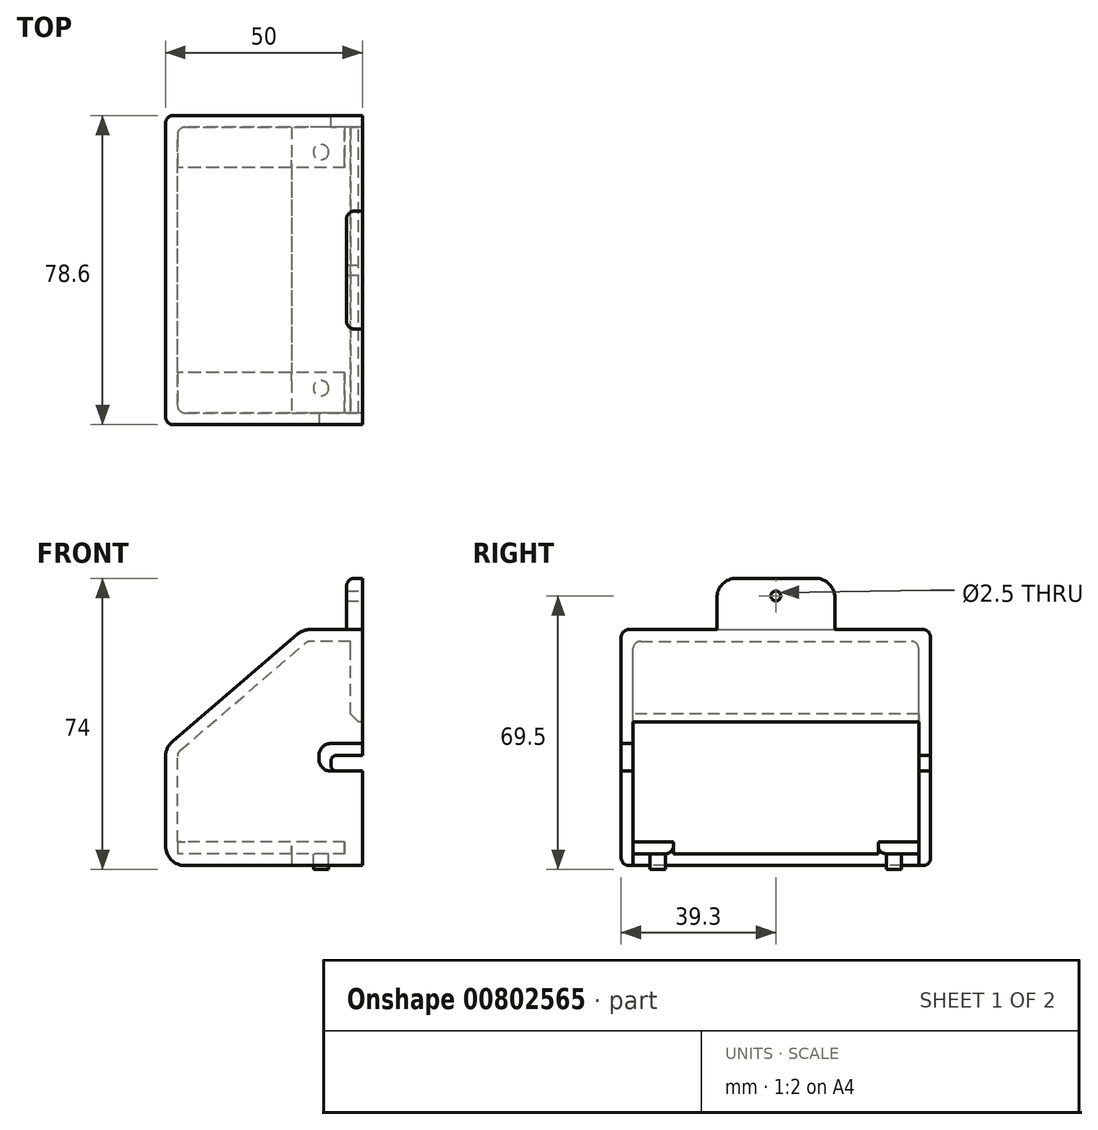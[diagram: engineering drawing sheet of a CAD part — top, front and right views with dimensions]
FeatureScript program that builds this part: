
annotation { "Feature Type Name" : "Feature", "Feature Type Description" : "" }
export const myFeature = defineFeature(function(context is Context, id is Id, definition is map)
    precondition{}
    {
        {
            var Q0;
            Q0=qCreatedBy(makeId("Front.planeOp"),FACE);
            var sketch = newSketch(context, id + "F0", { "sketchPlane" : qUnion([Q0])});
            skLineSegment(sketch, "E0", {"start": v(0, 0) * mm, "end": v(-50, 0) * mm});
            skLineSegment(sketch, "E1", {"start": v(-50, 0) * mm, "end": v(-50, 30) * mm});
            skLineSegment(sketch, "E2", {"start": v(0, 0) * mm, "end": v(0, 60) * mm});
            skLineSegment(sketch, "E3", {"start": v(0, 60) * mm, "end": v(-15, 60) * mm});
            skLineSegment(sketch, "E4", {"start": v(-50, 30) * mm, "end": v(-15, 60) * mm});
            skSolve(sketch);
        }
        {
            var Q0;
            Q0 = qSketchRegion(id + "F0", true);
            extrude(context, id + "F1", {"entities" : qUnion([Q0]), "depth" : 78.6 * mm, "offsetDistance" : 25 * mm});
        }
        {
            var Q0;
            Q0=qCreatedBy(makeId("Front.planeOp"),FACE);
            cPlane(context, id + "F2", {"entities" : qUnion([Q0]), "cplaneType" : CPlaneType.OFFSET, "offset" : 3 * mm, "width" : 150 * mm, "height" : 150 * mm});
        }
        {
            var Q0;
            Q0=qCreatedBy(id+"F2.planeOp",FACE);
            var sketch = newSketch(context, id + "F3", { "sketchPlane" : qUnion([Q0])});
            skLineSegment(sketch, "E5", {"start": v(0, 0) * mm, "end": v(0, 3) * mm, "construction": true});
            skLineSegment(sketch, "E6", {"start": v(0, 3) * mm, "end": v(-47, 3) * mm});
            skLineSegment(sketch, "E7", {"start": v(0, 3) * mm, "end": v(0, 36.5) * mm});
            skLineSegment(sketch, "E8", {"start": v(0, 36.5) * mm, "end": v(-3, 36.5) * mm});
            skLineSegment(sketch, "E9", {"start": v(-3, 36.5) * mm, "end": v(-3, 57) * mm});
            skLineSegment(sketch, "E10.0", {"start": v(-47, 28.62) * mm, "end": v(-13.9, 57) * mm});
            skLineSegment(sketch, "E11", {"start": v(-3, 57) * mm, "end": v(-13.9, 57) * mm});
            skLineSegment(sketch, "E12", {"start": v(-47, 3) * mm, "end": v(-47, 28.62) * mm});
            skPoint(sketch, "E13", {"position": v(-47, 28.62) * mm});
            skPoint(sketch, "E14", {"position": v(-13.9, 57) * mm});
            skSolve(sketch);
        }
        {
            var Q0;
            Q0 = qSketchRegion(id + "F3", true);
            extrude(context, id + "F4", {"entities" : qUnion([Q0]), "operationType" : NewBodyOperationType.REMOVE, "depth" : 72.6 * mm, "offsetDistance" : 25 * mm});
        }
        {
            var Q0;
            Q0=makeQuery(id+"F1.opExtrude","SWEPT_FACE",FACE,{"disambiguationData":[OSD([sQuery(id+"F0.wireOp",EDGE,"E0")])]});
            var sketch = newSketch(context, id + "F5", { "sketchPlane" : qUnion([Q0])});
            skLineSegment(sketch, "E15", {"start": v(0, 0) * mm, "end": v(0, 3) * mm, "construction": true});
            skLineSegment(sketch, "E16", {"start": v(0, 3) * mm, "end": v(-18, 3) * mm});
            skLineSegment(sketch, "E17", {"start": v(-18, 3) * mm, "end": v(-18, 75.6) * mm});
            skLineSegment(sketch, "E18", {"start": v(-18, 75.6) * mm, "end": v(0, 75.6) * mm});
            skLineSegment(sketch, "E19", {"start": v(0, 75.6) * mm, "end": v(0, 3) * mm});
            skSolve(sketch);
        }
        {
            var Q0;
            Q0 = qSketchRegion(id + "F5", true);
            extrude(context, id + "F6", {"entities" : qUnion([Q0]), "operationType" : NewBodyOperationType.REMOVE, "oppositeDirection" : true, "depth" : 5 * mm, "offsetDistance" : 25 * mm});
        }
        {
            var Q0;
            Q0=qCreatedBy(makeId("Front.planeOp"),FACE);
            var sketch = newSketch(context, id + "F7", { "sketchPlane" : qUnion([Q0])});
            skLineSegment(sketch, "E20", {"start": v(0, 0) * mm, "end": v(0, 24) * mm, "construction": true});
            skLineSegment(sketch, "E21", {"start": v(0, 24) * mm, "end": v(0, 28) * mm});
            skLineSegment(sketch, "E22", {"start": v(0, 28) * mm, "end": v(-6.5, 28) * mm});
            skLineSegment(sketch, "E23", {"start": v(-8, 26.5) * mm, "end": v(-8, 25.5) * mm});
            skLineSegment(sketch, "E24", {"start": v(-6.5, 24) * mm, "end": v(0, 24) * mm});
            skPoint(sketch, "E25.visualSharp", {"position": v(-8, 28) * mm});
            skArc(sketch, "E25.filletArc", {"start": v(-6.5, 28) * mm, "mid": v(-7.56, 27.56) * mm, "end": v(-8, 26.5) * mm});
            skPoint(sketch, "E26.visualSharp", {"position": v(-8, 24) * mm});
            skArc(sketch, "E26.filletArc", {"start": v(-8, 25.5) * mm, "mid": v(-7.56, 24.44) * mm, "end": v(-6.5, 24) * mm});
            skSolve(sketch);
        }
        {
            var Q0;
            Q0 = qSketchRegion(id + "F7", true);
            extrude(context, id + "F8", {"entities" : qUnion([Q0]), "operationType" : NewBodyOperationType.REMOVE, "depth" : 5 * mm, "offsetDistance" : 25 * mm});
        }
        {
            var Q0;
            Q0=makeQuery(id+"F1.opExtrude","CAP_FACE",FACE,{"disambiguationData":[OSD([sQuery(id+"F0.wireOp",EDGE,"E0"),sQuery(id+"F0.wireOp",EDGE,"E1"),sQuery(id+"F0.wireOp",EDGE,"E2"),sQuery(id+"F0.wireOp",EDGE,"E3"),sQuery(id+"F0.wireOp",EDGE,"E4")])],"isStart":false});
            var sketch = newSketch(context, id + "F9", { "sketchPlane" : qUnion([Q0])});
            skLineSegment(sketch, "E27", {"start": v(0, 0) * mm, "end": v(0, 24) * mm, "construction": true});
            skLineSegment(sketch, "E28", {"start": v(0, 24) * mm, "end": v(0, 31) * mm});
            skLineSegment(sketch, "E29", {"start": v(0, 31) * mm, "end": v(-8, 31) * mm});
            skLineSegment(sketch, "E30", {"start": v(-11, 28) * mm, "end": v(-11, 27) * mm});
            skLineSegment(sketch, "E31", {"start": v(-8, 24) * mm, "end": v(0, 24) * mm});
            skPoint(sketch, "E32.visualSharp", {"position": v(-11, 31) * mm});
            skArc(sketch, "E32.filletArc", {"start": v(-8, 31) * mm, "mid": v(-10.12, 30.12) * mm, "end": v(-11, 28) * mm});
            skPoint(sketch, "E33.visualSharp", {"position": v(-11, 24) * mm});
            skArc(sketch, "E33.filletArc", {"start": v(-11, 27) * mm, "mid": v(-10.12, 24.88) * mm, "end": v(-8, 24) * mm});
            skSolve(sketch);
        }
        {
            var Q0;
            Q0 = qSketchRegion(id + "F9", true);
            extrude(context, id + "F10", {"entities" : qUnion([Q0]), "operationType" : NewBodyOperationType.REMOVE, "oppositeDirection" : true, "depth" : 5 * mm, "offsetDistance" : 25 * mm});
        }
        {
            var Q0;
            Q0=makeQuery(id+"F1.opExtrude","SWEPT_FACE",FACE,{"disambiguationData":[OSD([sQuery(id+"F0.wireOp",EDGE,"E3")])]});
            var sketch = newSketch(context, id + "F11", { "sketchPlane" : qUnion([Q0])});
            skLineSegment(sketch, "E34", {"start": v(0, 0) * mm, "end": v(0, -39.3) * mm, "construction": true});
            skLineSegment(sketch, "E35", {"start": v(0, -39.3) * mm, "end": v(-4, -39.3) * mm, "construction": true});
            skLineSegment(sketch, "E36", {"start": v(-4, -39.3) * mm, "end": v(-4, -24.3) * mm});
            skLineSegment(sketch, "E37", {"start": v(-4, -24.3) * mm, "end": v(0, -24.3) * mm});
            skLineSegment(sketch, "E38", {"start": v(0, -24.3) * mm, "end": v(0, -39.3) * mm});
            skLineSegment(sketch, "E39", {"start": v(-4, -39.3) * mm, "end": v(-4, -54.3) * mm});
            skLineSegment(sketch, "E40", {"start": v(-4, -54.3) * mm, "end": v(0, -54.3) * mm});
            skLineSegment(sketch, "E41", {"start": v(0, -54.3) * mm, "end": v(0, -24.3) * mm});
            skSolve(sketch);
        }
        {
            var Q0;
            Q0 = qSketchRegion(id + "F11", true);
            extrude(context, id + "F12", {"entities" : qUnion([Q0]), "operationType" : NewBodyOperationType.ADD, "depth" : 13 * mm, "offsetDistance" : 25 * mm});
        }
        {
            var Q0;
            Q0=makeQuery(id+"F12.opExtrude","CAP_EDGE",EDGE,{"disambiguationData":[OSD([sQuery(id+"F11.wireOp",EDGE,"E40")])],"isStart":false});
            var Q1;
            Q1=makeQuery(id+"F12.opExtrude","CAP_EDGE",EDGE,{"disambiguationData":[OSD([sQuery(id+"F11.wireOp",EDGE,"E37")])],"isStart":false});
            var Q2;
            Q2=makeQuery(id+"F1.opExtrude","SWEPT_EDGE",EDGE,{"disambiguationData":[OSD([sQuery(id+"F0.wireOp",EDGE,"E3"),sQuery(id+"F0.wireOp",EDGE,"E4")])]});
            var Q3;
            Q3=makeQuery(id+"F1.opExtrude","SWEPT_EDGE",EDGE,{"disambiguationData":[OSD([sQuery(id+"F0.wireOp",EDGE,"E1"),sQuery(id+"F0.wireOp",EDGE,"E4")])]});
            var Q4;
            Q4=makeQuery(id+"F1.opExtrude","SWEPT_EDGE",EDGE,{"disambiguationData":[OSD([sQuery(id+"F0.wireOp",EDGE,"E0"),sQuery(id+"F0.wireOp",EDGE,"E1")])]});
            fillet(context, id + "F13", {"entities" : qUnion([Q0, Q1, Q2, Q3, Q4]), "radius" : 5 * mm, "tangentPropagation" : true, "allowEdgeOverflow" : false});
        }
        {
            var Q0;
            Q0=makeQuery(id+"F12.opExtrude","SWEPT_EDGE",EDGE,{"disambiguationData":[OSD([sQuery(id+"F11.wireOp",EDGE,"E39"),sQuery(id+"F11.wireOp",EDGE,"E40")])]});
            var Q1;
            Q1=makeQuery(id+"F1.opExtrude","CAP_EDGE",EDGE,{"disambiguationData":[OSD([sQuery(id+"F0.wireOp",EDGE,"E4")])],"isStart":true});
            var Q2;
            Q2=makeQuery(id+"F1.opExtrude","CAP_EDGE",EDGE,{"disambiguationData":[OSD([sQuery(id+"F0.wireOp",EDGE,"E4")])],"isStart":false});
            fillet(context, id + "F14", {"entities" : qUnion([Q0, Q1, Q2]), "radius" : 2 * mm, "tangentPropagation" : true, "allowEdgeOverflow" : false});
        }
        {
            var Q0;
            {var subQ0=sQuery(id+"F0.wireOp",EDGE,"E3");var subQ1=makeQuery(id+"F1.opExtrude","SWEPT_FACE",FACE,{"disambiguationData":[OSD([subQ0])]});var subQ3=sQuery(id+"F0.wireOp",EDGE,"E2");Q0=makeQuery(id+"F12.boolean.opBoolean","MERGE",FACE,{"derivedFrom":[makeQuery(id+"F10.boolean.opBoolean","SPLIT",FACE,{"disambiguationData":[TD([subQ1])],"derivedFrom":makeQuery(id+"F8.boolean.opBoolean","SPLIT",FACE,{"disambiguationData":[TD([subQ1])],"derivedFrom":makeQuery(id+"F1.opExtrude","SWEPT_FACE",FACE,{"disambiguationData":[OSD([subQ3])]})})}),makeQuery(id+"F12.opExtrude","SWEPT_FACE",FACE,{"disambiguationData":[OSD([sQuery(id+"F11.wireOp",EDGE,"E41")])]})]});}
            var sketch = newSketch(context, id + "F15", { "sketchPlane" : qUnion([Q0])});
            skLineSegment(sketch, "E42", {"start": v(-39.3, 73) * mm, "end": v(-39.3, 68.5) * mm, "construction": true});
            skLineSegment(sketch, "E43", {"start": v(-39.3, 68.5) * mm, "end": v(-24.3, 68.5) * mm, "construction": true});
            skCircle(sketch, "E44", {"center": v(-39.3, 68.5) * mm, "radius": 1.25 * mm});
            skSolve(sketch);
        }
        {
            var Q0;
            Q0 = qSketchRegion(id + "F15", true);
            extrude(context, id + "F16", {"entities" : qUnion([Q0]), "operationType" : NewBodyOperationType.REMOVE, "oppositeDirection" : true, "depth" : 25 * mm, "offsetDistance" : 25 * mm});
        }
        {
            var Q0;
            Q0=makeQuery(id+"F4.boolean.opBoolean","COPY",FACE,{"derivedFrom":makeQuery(id+"F4.opExtrude","SWEPT_FACE",FACE,{"disambiguationData":[OSD([sQuery(id+"F3.wireOp",EDGE,"E12")])]})});
            var sketch = newSketch(context, id + "F17", { "sketchPlane" : qUnion([Q0])});
            skLineSegment(sketch, "E45", {"start": v(0, 0) * mm, "end": v(-3, 0) * mm, "construction": true});
            skLineSegment(sketch, "E46", {"start": v(-75.6, 0) * mm, "end": v(-78.6, 0) * mm, "construction": true});
            skLineSegment(sketch, "E47", {"start": v(-3, 0) * mm, "end": v(-39.3, 0) * mm, "construction": true});
            skLineSegment(sketch, "E48", {"start": v(-39.3, 0) * mm, "end": v(-39.3, 3) * mm, "construction": true});
            skLineSegment(sketch, "E49", {"start": v(-39.3, 3) * mm, "end": v(-39.3, 6) * mm, "construction": true});
            skLineSegment(sketch, "E50", {"start": v(-39.3, 6) * mm, "end": v(-3, 6) * mm, "construction": true});
            skLineSegment(sketch, "E51", {"start": v(-3, 6) * mm, "end": v(-13.3, 6) * mm});
            skLineSegment(sketch, "E52", {"start": v(-13.3, 6) * mm, "end": v(-13.3, 3) * mm});
            skLineSegment(sketch, "E53", {"start": v(-13.3, 3) * mm, "end": v(-3, 3) * mm});
            skLineSegment(sketch, "E54", {"start": v(-3, 3) * mm, "end": v(-3, 6) * mm});
            skLineSegment(sketch, "E55.MirrorCS", {"start": v(-75.6, 3) * mm, "end": v(-75.6, 6) * mm});
            skLineSegment(sketch, "E56.MirrorCS", {"start": v(-65.3, 6) * mm, "end": v(-65.3, 3) * mm});
            skLineSegment(sketch, "E57.MirrorCS", {"start": v(-65.3, 3) * mm, "end": v(-75.6, 3) * mm});
            skLineSegment(sketch, "E58", {"start": v(-65.3, 6) * mm, "end": v(-75.6, 6) * mm});
            skSolve(sketch);
        }
        {
            var Q0;
            Q0 = qSketchRegion(id + "F17", true);
            extrude(context, id + "F18", {"entities" : qUnion([Q0]), "operationType" : NewBodyOperationType.ADD, "depth" : 42.5 * mm, "offsetDistance" : 25 * mm});
        }
        {
            var Q0;
            Q0=qCreatedBy(makeId("Top.planeOp"),FACE);
            cPlane(context, id + "F19", {"entities" : qUnion([Q0]), "cplaneType" : CPlaneType.OFFSET, "offset" : 3 * mm, "width" : 150 * mm, "height" : 150 * mm});
        }
        {
            var Q0;
            Q0=qCreatedBy(id+"F19.planeOp",FACE);
            var sketch = newSketch(context, id + "F20", { "sketchPlane" : qUnion([Q0])});
            skLineSegment(sketch, "E59", {"start": v(0, 0) * mm, "end": v(0, -3) * mm, "construction": true});
            skLineSegment(sketch, "E60", {"start": v(0, -3) * mm, "end": v(-4, -3) * mm, "construction": true});
            skLineSegment(sketch, "E61", {"start": v(-4, -3) * mm, "end": v(-10.5, -3) * mm, "construction": true});
            skLineSegment(sketch, "E62", {"start": v(-10.5, -3) * mm, "end": v(-10.5, -3.3) * mm, "construction": true});
            skLineSegment(sketch, "E63", {"start": v(-10.5, -3.3) * mm, "end": v(-10.5, -9.3) * mm, "construction": true});
            skLineSegment(sketch, "E64", {"start": v(-10.5, -9.3) * mm, "end": v(-10.5, -69.3) * mm, "construction": true});
            skLineSegment(sketch, "E65", {"start": v(-10.5, -69.3) * mm, "end": v(-10.5, -75.3) * mm, "construction": true});
            skLineSegment(sketch, "E66", {"start": v(-10.5, -75.3) * mm, "end": v(-10.5, -75.6) * mm, "construction": true});
            skLineSegment(sketch, "E67", {"start": v(-10.5, -75.6) * mm, "end": v(-10.5, -78.6) * mm, "construction": true});
            skCircle(sketch, "E68", {"center": v(-10.5, -9.3) * mm, "radius": 1.95 * mm});
            skCircle(sketch, "E69", {"center": v(-10.5, -69.3) * mm, "radius": 1.95 * mm});
            skLineSegment(sketch, "E70", {"start": v(-10.5, -3) * mm, "end": v(-14, -3) * mm, "construction": true});
            skLineSegment(sketch, "E71", {"start": v(-14, -3) * mm, "end": v(-18, -3) * mm, "construction": true});
            skSolve(sketch);
        }
        {
            var Q0;
            Q0 = qSketchRegion(id + "F20", true);
            extrude(context, id + "F21", {"entities" : qUnion([Q0]), "operationType" : NewBodyOperationType.ADD, "oppositeDirection" : true, "depth" : 4 * mm, "offsetDistance" : 25 * mm});
        }
        {
            var Q0;
            Q0=makeQuery(id+"F4.boolean.opBoolean","COPY",EDGE,{"derivedFrom":makeQuery(id+"F4.opExtrude","SWEPT_EDGE",EDGE,{"disambiguationData":[OSD([sQuery(id+"F3.wireOp",EDGE,"E8"),sQuery(id+"F3.wireOp",EDGE,"E9")])]})});
            chamfer(context, id + "F22", {"entities" : qUnion([Q0]), "width" : 2 * mm, "tangentPropagation" : true});
        }
        {
            var Q0;
            Q0=makeQuery(id+"F18.opExtrude","CAP_EDGE",EDGE,{"disambiguationData":[OSD([sQuery(id+"F17.wireOp",EDGE,"E51")])],"isStart":true});
            var Q1;
            Q1=makeQuery(id+"F18.opExtrude","CAP_EDGE",EDGE,{"disambiguationData":[OSD([sQuery(id+"F17.wireOp",EDGE,"E52")])],"isStart":true});
            var Q2;
            {var subQ0=sQuery(id+"F3.wireOp",EDGE,"E6");var subQ1=sQuery(id+"F17.wireOp",EDGE,"E52");Q2=makeQuery(id+"F18.boolean.opBoolean","SPLIT",EDGE,{"disambiguationData":[topologyDisambiguationEdgeConnected([makeQuery(id+"F4.boolean.opBoolean","COPY",FACE,{"derivedFrom":makeQuery(id+"F4.opExtrude","SWEPT_FACE",FACE,{"disambiguationData":[OSD([subQ0])]})})])],"derivedFrom":makeQuery(id+"F18.opExtrude","SWEPT_EDGE",EDGE,{"disambiguationData":[OSD([subQ0,sQuery(id+"F3.wireOp",EDGE,"E12"),subQ1,sQuery(id+"F17.wireOp",EDGE,"E53")])]})});}
            var Q3;
            Q3=makeQuery(id+"F18.opExtrude","CAP_EDGE",EDGE,{"disambiguationData":[OSD([sQuery(id+"F17.wireOp",EDGE,"E58")])],"isStart":true});
            var Q4;
            Q4=makeQuery(id+"F18.opExtrude","CAP_EDGE",EDGE,{"disambiguationData":[OSD([sQuery(id+"F17.wireOp",EDGE,"E56.MirrorCS")])],"isStart":true});
            var Q5;
            {var subQ0=sQuery(id+"F3.wireOp",EDGE,"E6");var subQ1=sQuery(id+"F17.wireOp",EDGE,"E56.MirrorCS");Q5=makeQuery(id+"F18.boolean.opBoolean","SPLIT",EDGE,{"disambiguationData":[topologyDisambiguationEdgeConnected([makeQuery(id+"F4.boolean.opBoolean","COPY",FACE,{"derivedFrom":makeQuery(id+"F4.opExtrude","SWEPT_FACE",FACE,{"disambiguationData":[OSD([subQ0])]})})])],"derivedFrom":makeQuery(id+"F18.opExtrude","SWEPT_EDGE",EDGE,{"disambiguationData":[OSD([subQ0,sQuery(id+"F3.wireOp",EDGE,"E12"),subQ1,sQuery(id+"F17.wireOp",EDGE,"E57.MirrorCS")])]})});}
            var Q6;
            Q6=makeQuery(id+"F18.opExtrude","SWEPT_EDGE",EDGE,{"disambiguationData":[OSD([sQuery(id+"F3.wireOp",EDGE,"E12"),sQuery(id+"F17.wireOp",EDGE,"E55.MirrorCS"),sQuery(id+"F17.wireOp",EDGE,"E58")])]});
            var Q7;
            Q7=makeQuery(id+"F18.opExtrude","SWEPT_EDGE",EDGE,{"disambiguationData":[OSD([sQuery(id+"F3.wireOp",EDGE,"E12"),sQuery(id+"F17.wireOp",EDGE,"E51"),sQuery(id+"F17.wireOp",EDGE,"E54")])]});
            var Q8;
            Q8=makeQuery(id+"F4.boolean.opBoolean","COPY",EDGE,{"derivedFrom":makeQuery(id+"F4.opExtrude","CAP_EDGE",EDGE,{"disambiguationData":[OSD([sQuery(id+"F3.wireOp",EDGE,"E12")])],"isStart":true})});
            var Q9;
            Q9=makeQuery(id+"F4.boolean.opBoolean","COPY",EDGE,{"derivedFrom":makeQuery(id+"F4.opExtrude","CAP_EDGE",EDGE,{"disambiguationData":[OSD([sQuery(id+"F3.wireOp",EDGE,"E10.0")])],"isStart":true})});
            var Q10;
            Q10=makeQuery(id+"F4.boolean.opBoolean","COPY",EDGE,{"derivedFrom":makeQuery(id+"F4.opExtrude","SWEPT_EDGE",EDGE,{"disambiguationData":[OSD([sQuery(id+"F3.wireOp",EDGE,"E10.0"),sQuery(id+"F3.wireOp",EDGE,"E12")])]})});
            var Q11;
            Q11=makeQuery(id+"F4.boolean.opBoolean","COPY",EDGE,{"derivedFrom":makeQuery(id+"F4.opExtrude","CAP_EDGE",EDGE,{"disambiguationData":[OSD([sQuery(id+"F3.wireOp",EDGE,"E12")])],"isStart":false})});
            var Q12;
            Q12=makeQuery(id+"F4.boolean.opBoolean","COPY",EDGE,{"derivedFrom":makeQuery(id+"F4.opExtrude","CAP_EDGE",EDGE,{"disambiguationData":[OSD([sQuery(id+"F3.wireOp",EDGE,"E10.0")])],"isStart":false})});
            var Q13;
            Q13=makeQuery(id+"F4.boolean.opBoolean","COPY",EDGE,{"derivedFrom":makeQuery(id+"F4.opExtrude","SWEPT_EDGE",EDGE,{"disambiguationData":[OSD([sQuery(id+"F3.wireOp",EDGE,"E10.0"),sQuery(id+"F3.wireOp",EDGE,"E11")])]})});
            var Q14;
            Q14=makeQuery(id+"F4.boolean.opBoolean","COPY",EDGE,{"derivedFrom":makeQuery(id+"F4.opExtrude","CAP_EDGE",EDGE,{"disambiguationData":[OSD([sQuery(id+"F3.wireOp",EDGE,"E11")])],"isStart":true})});
            var Q15;
            Q15=makeQuery(id+"F4.boolean.opBoolean","COPY",EDGE,{"derivedFrom":makeQuery(id+"F4.opExtrude","CAP_EDGE",EDGE,{"disambiguationData":[OSD([sQuery(id+"F3.wireOp",EDGE,"E11")])],"isStart":false})});
            fillet(context, id + "F23", {"entities" : qUnion([Q0, Q1, Q2, Q3, Q4, Q5, Q6, Q7, Q8, Q9, Q10, Q11, Q12, Q13, Q14, Q15]), "radius" : 2 * mm, "tangentPropagation" : true, "allowEdgeOverflow" : false});
        }
    });
